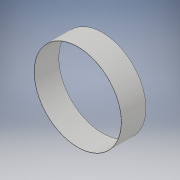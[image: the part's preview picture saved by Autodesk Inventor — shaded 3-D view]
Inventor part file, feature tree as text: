
AUTODESK INVENTOR PART (.ipt)
format: ipt  version: 2019 (Build 230136000, 136)  size: 104,960 bytes
history: native  units: mm
features: extrude x2, sketch x2
ambient origin geometry x8: Origin, YZ Plane, XZ Plane, XY Plane, X Axis, Y Axis, Z Axis, Center Point
bodies: Solid1 (feature_tree)
feature tree (4):
  extrude  "Extrusion1"  Depth=116.5mm TaperAngle=0.0deg
  extrude  "Extrusion2"  Depth=11.65mm TaperAngle=0.0deg
  sketch  "Sketch1"  dims[d0=416.68mm d1=116.5mm d2=0.0mm]
  sketch  "Sketch2"  dims[d3=414.0mm d4=11.65mm d5=0.0mm]
